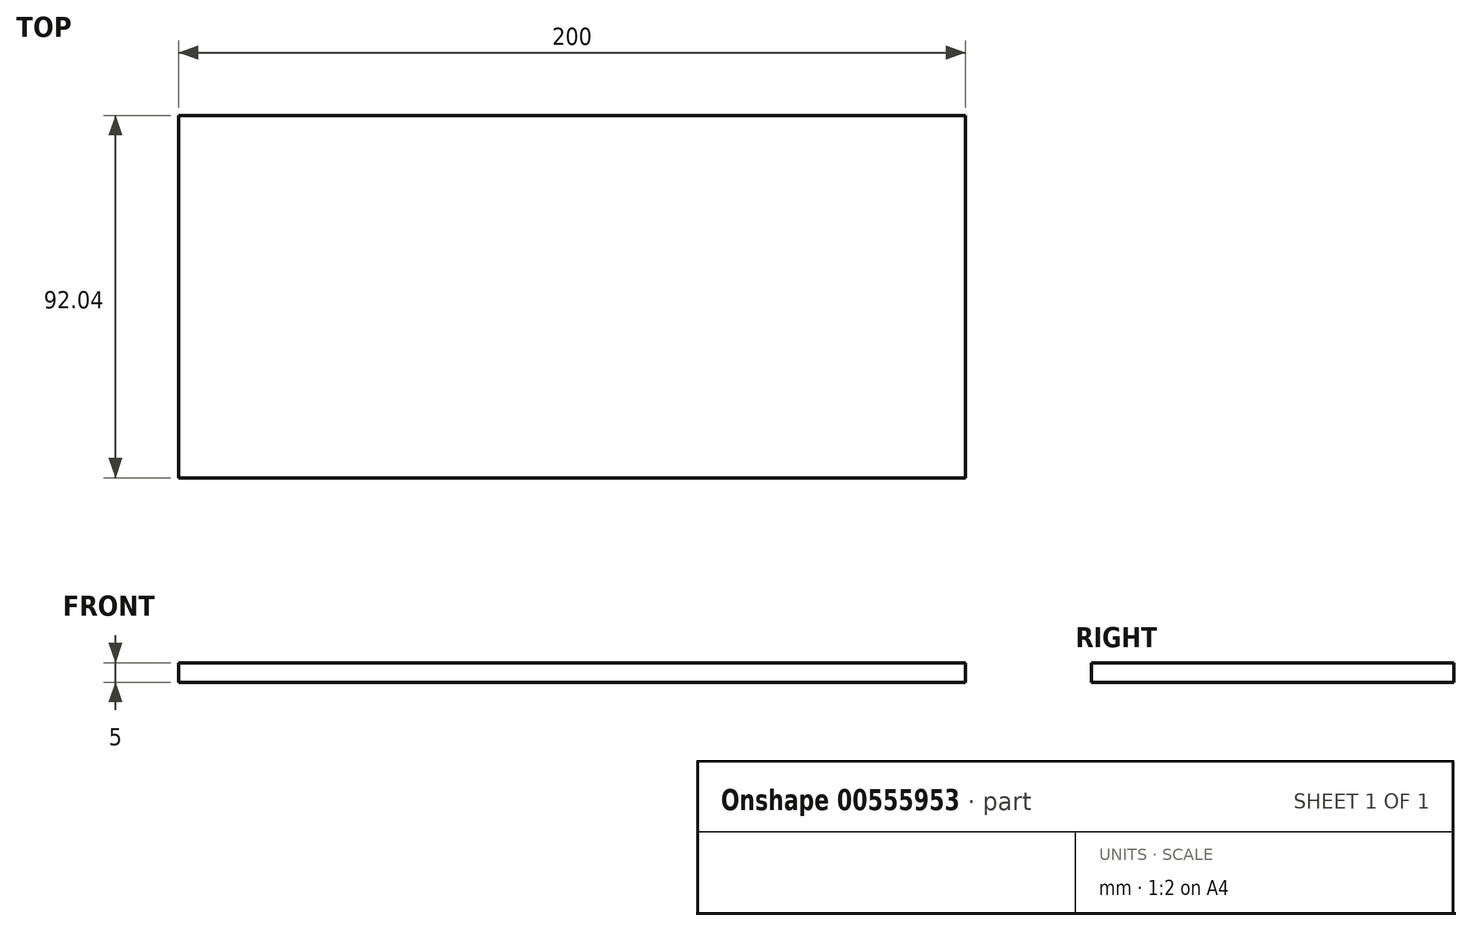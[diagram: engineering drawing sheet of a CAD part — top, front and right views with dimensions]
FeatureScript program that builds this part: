
annotation { "Feature Type Name" : "Feature", "Feature Type Description" : "" }
export const myFeature = defineFeature(function(context is Context, id is Id, definition is map)
    precondition{}
    {
        {
            var Q0;
            Q0=qCreatedBy(makeId("Top.planeOp"),FACE);
            var sketch = newSketch(context, id + "F0", { "sketchPlane" : qUnion([Q0])});
            skLineSegment(sketch, "E0.bottom", {"start": v(100, 46.02) * mm, "end": v(-100, 46.02) * mm});
            skLineSegment(sketch, "E0.top", {"start": v(100, -46.02) * mm, "end": v(-100, -46.02) * mm});
            skLineSegment(sketch, "E0.left", {"start": v(100, 46.02) * mm, "end": v(100, -46.02) * mm});
            skLineSegment(sketch, "E0.right", {"start": v(-100, 46.02) * mm, "end": v(-100, -46.02) * mm});
            skPoint(sketch, "E0.middle", {"position": v(0, 0) * mm});
            skSolve(sketch);
        }
        {
            var Q0;
            Q0=makeQuery(id+"F0.imprint","IMPRINT",FACE,{"disambiguationData":[TD([[makeQuery(id+"F0.imprint","IMPRINT",EDGE,{"derivedFrom":sQuery(id+"F0.wireOp",EDGE,"E0.bottom")}),1.0]])]});
            extrude(context, id + "F1", {"entities" : qUnion([Q0]), "depth" : 5 * mm, "offsetDistance" : 25.4 * mm});
        }
    });
